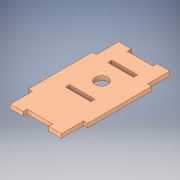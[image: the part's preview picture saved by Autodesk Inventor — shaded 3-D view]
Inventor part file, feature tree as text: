
AUTODESK INVENTOR PART (.ipt)
format: ipt  version: 2019 (Build 230136000, 136)  size: 160,256 bytes
history: native  units: mm
features: extrude x1, sketch x1
ambient origin geometry x8: Origin, YZ Plane, XZ Plane, XY Plane, X Axis, Y Axis, Z Axis, Center Point
bodies: Body1 (feature_tree)
feature tree (2):
  extrude  "Extrusión2"  Depth=40.0mm
  sketch  "Boceto1"  dims[d0=10.0mm d1=40.0mm d2=20.0mm d3=33.36mm d5=0.0mm d6=3.18mm d7=20.0mm d8=3.18mm d9=20.0mm d10=0.0mm d11=12.0mm d12=3.18mm d13=20.0mm d14=3.18mm d15=20.0mm d16=0.0mm d17=0.0mm d18=30.0mm d19=30.0mm d20=3.18mm d21=50.0mm d22=42.36mm d23=3.18mm d24=50.0mm d25=42.36mm d28=3.18mm d29=0.0mm]
